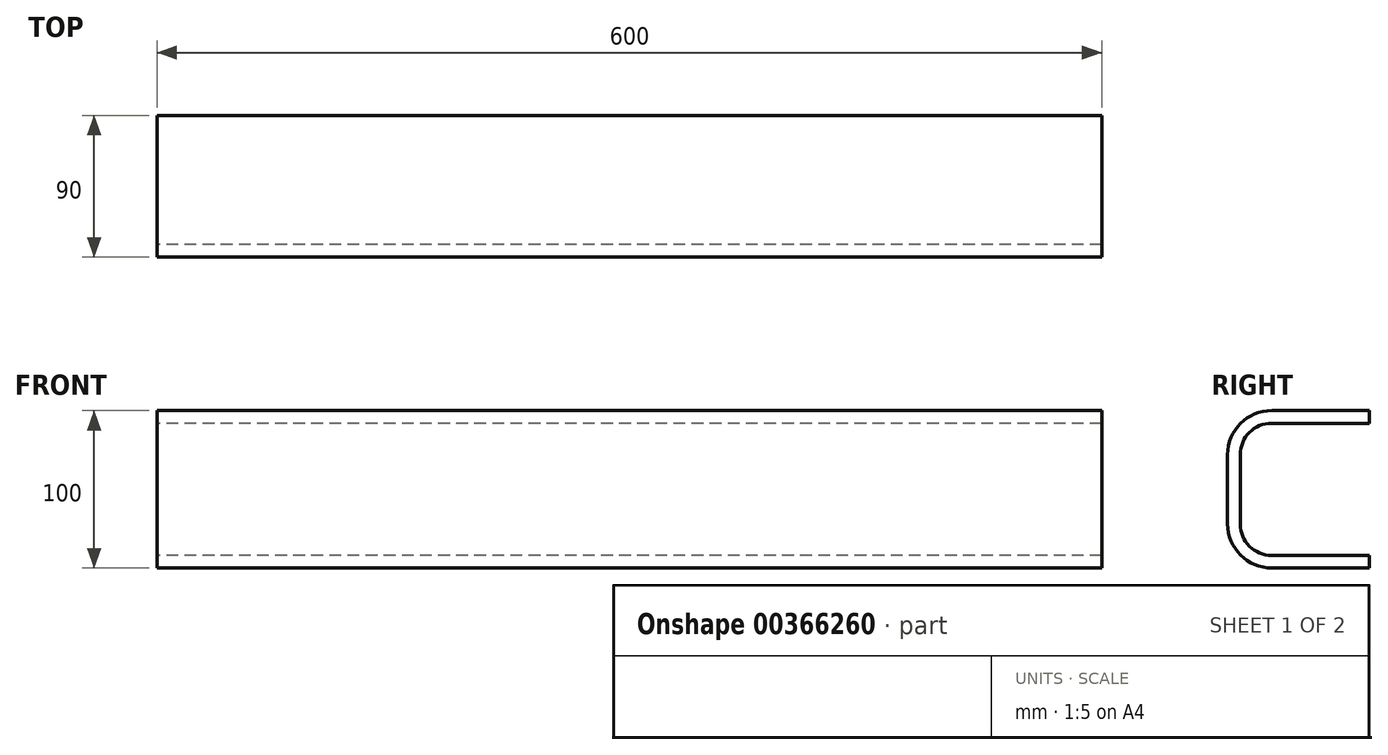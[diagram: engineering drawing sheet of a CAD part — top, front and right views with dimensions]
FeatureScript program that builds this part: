
annotation { "Feature Type Name" : "Feature", "Feature Type Description" : "" }
export const myFeature = defineFeature(function(context is Context, id is Id, definition is map)
    precondition{}
    {
        {
            var Q0;
            Q0=qCreatedBy(makeId("Right.planeOp"),FACE);
            var sketch = newSketch(context, id + "F0", { "sketchPlane" : qUnion([Q0])});
            skLineSegment(sketch, "E0", {"start": v(90, 50) * mm, "end": v(28, 50) * mm});
            skLineSegment(sketch, "E1", {"start": v(0, 22) * mm, "end": v(0, -22) * mm});
            skLineSegment(sketch, "E2", {"start": v(28, -50) * mm, "end": v(90, -50) * mm});
            skLineSegment(sketch, "E3", {"start": v(90, -50) * mm, "end": v(90, -42) * mm});
            skLineSegment(sketch, "E4", {"start": v(90, -42) * mm, "end": v(28, -42) * mm});
            skLineSegment(sketch, "E5", {"start": v(8, -22) * mm, "end": v(8, 22) * mm});
            skLineSegment(sketch, "E6", {"start": v(28, 42) * mm, "end": v(90, 42) * mm});
            skLineSegment(sketch, "E7", {"start": v(90, 42) * mm, "end": v(90, 50) * mm});
            skPoint(sketch, "E8.visualSharp", {"position": v(8, 42) * mm});
            skArc(sketch, "E8.filletArc", {"start": v(28, 42) * mm, "mid": v(13.86, 36.14) * mm, "end": v(8, 22) * mm});
            skPoint(sketch, "E9.visualSharp", {"position": v(8, -42) * mm});
            skArc(sketch, "E9.filletArc", {"start": v(8, -22) * mm, "mid": v(13.86, -36.14) * mm, "end": v(28, -42) * mm});
            skPoint(sketch, "E10.visualSharp", {"position": v(0, 50) * mm});
            skArc(sketch, "E10.filletArc", {"start": v(28, 50) * mm, "mid": v(8.2, 41.8) * mm, "end": v(0, 22) * mm});
            skPoint(sketch, "E11.visualSharp", {"position": v(0, -50) * mm});
            skArc(sketch, "E11.filletArc", {"start": v(0, -22) * mm, "mid": v(8.2, -41.8) * mm, "end": v(28, -50) * mm});
            skSolve(sketch);
        }
        {
            var Q0;
            Q0 = qSketchRegion(id + "F0", true);
            extrude(context, id + "F1", {"entities" : qUnion([Q0]), "depth" : 600 * mm});
        }
    });
